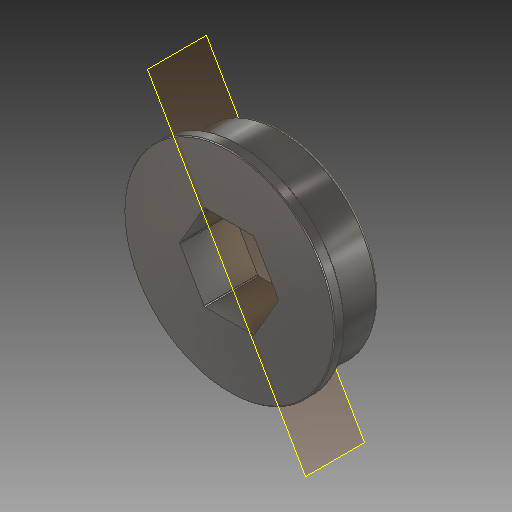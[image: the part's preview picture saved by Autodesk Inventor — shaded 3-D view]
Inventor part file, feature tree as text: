
AUTODESK INVENTOR PART (.ipt)
format: ipt  version: 2018 (Build 220112000, 112)  size: 168,448 bytes
history: native  units: in
note: dims shown in document units (in); Inventor stores cm internally (conversion verified against a paired STEP export)
features: plane x1, fillet x1
ambient origin geometry x8: Origin, YZ Plane, XZ Plane, XY Plane, X Axis, Y Axis, Z Axis, Center Point
bodies: Solid1 (feature_tree)
feature tree (2):
  plane  "Work Plane1"
  fillet  "Fillet2"  [1 undecoded]
note: 1 required parameter value undecoded (feature->parameter linkage not recoverable at this tier; creation-order binding heuristic only, values carry confidence <= 0.55)
